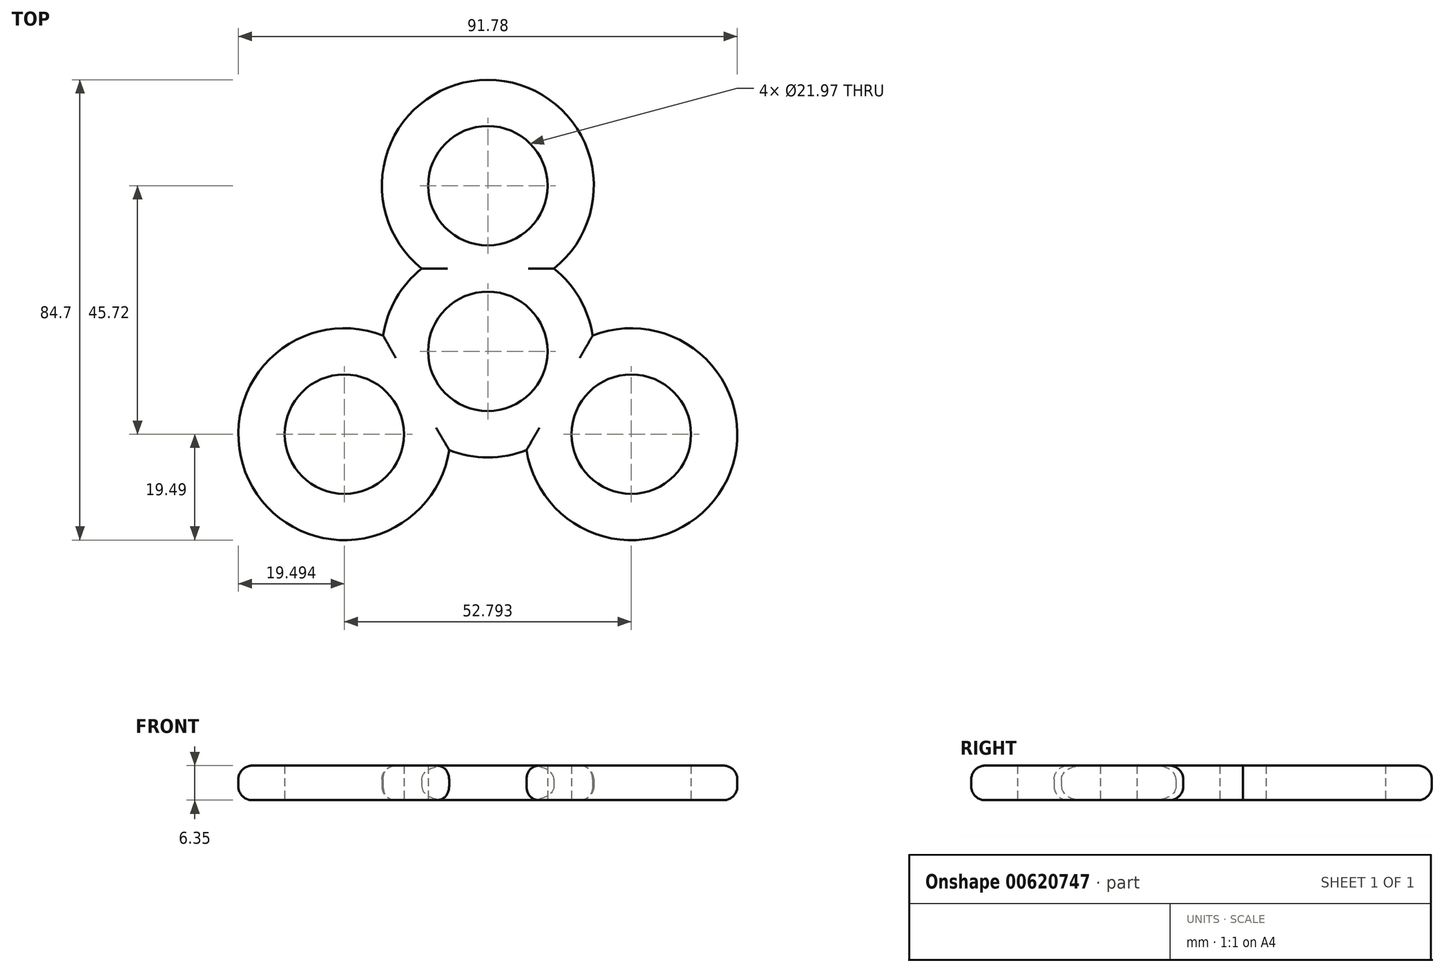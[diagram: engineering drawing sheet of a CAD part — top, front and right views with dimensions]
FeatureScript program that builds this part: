
annotation { "Feature Type Name" : "Feature", "Feature Type Description" : "" }
export const myFeature = defineFeature(function(context is Context, id is Id, definition is map)
    precondition{}
    {
        {
            var Q0;
            Q0=qCreatedBy(makeId("Top.planeOp"),FACE);
            var sketch = newSketch(context, id + "F0", { "sketchPlane" : qUnion([Q0])});
            skCircle(sketch, "E0", {"center": v(0, 0) * mm, "radius": 10.99 * mm});
            skLineSegment(sketch, "E1", {"start": v(0, 0) * mm, "end": v(0, 30.48) * mm});
            skLineSegment(sketch, "E2", {"start": v(0, 0) * mm, "end": v(-26.4, -15.24) * mm});
            skLineSegment(sketch, "E3", {"start": v(0, 0) * mm, "end": v(26.4, -15.24) * mm});
            skCircle(sketch, "E4", {"center": v(-26.4, -15.24) * mm, "radius": 10.99 * mm});
            skCircle(sketch, "E5", {"center": v(0, 30.48) * mm, "radius": 10.99 * mm});
            skCircle(sketch, "E6", {"center": v(26.4, -15.24) * mm, "radius": 10.99 * mm});
            skCircle(sketch, "E7", {"center": v(0, 0) * mm, "radius": 19.5 * mm});
            skCircle(sketch, "E8", {"center": v(-26.4, -15.24) * mm, "radius": 19.5 * mm});
            skCircle(sketch, "E9", {"center": v(26.4, -15.24) * mm, "radius": 19.5 * mm});
            skCircle(sketch, "E10", {"center": v(0, 30.48) * mm, "radius": 0.5 * mm});
            skCircle(sketch, "E11", {"center": v(0, 30.48) * mm, "radius": 19.5 * mm});
            skSolve(sketch);
        }
        {
            var Q0;
            Q0 = qSketchRegion(id + "F0", true);
            extrude(context, id + "F1", {"entities" : qUnion([Q0]), "depth" : 6.35 * mm, "offsetDistance" : 25.4 * mm});
        }
        {
            var Q0;
            Q0=makeQuery(id+"F1.opExtrude","CAP_EDGE",EDGE,{"disambiguationData":[OSD([sQuery(id+"F0.wireOp",EDGE,"E11")])],"isStart":false});
            var Q1;
            Q1=makeQuery(id+"F1.opExtrude","CAP_EDGE",EDGE,{"disambiguationData":[OSD([sQuery(id+"F0.wireOp",EDGE,"E8")])],"isStart":false});
            var Q2;
            {var subQ0=sQuery(id+"F0.wireOp",EDGE,"E7");Q2=makeQuery(id+"F1.opExtrude","CAP_EDGE",EDGE,{"disambiguationData":[OSD([subQ0]),TDD([makeQuery(id+"F0.imprint","IMPRINT",EDGE,{"disambiguationData":[TD([[makeQuery(id+"F0.imprint","INTERSECT",VERTEX,{"disambiguationData":[OD(1.0)],"derivedFrom":[subQ0,sQuery(id+"F0.wireOp",EDGE,"E8")]}),-1.0]])],"derivedFrom":subQ0})])],"isStart":false});}
            var Q3;
            {var subQ0=sQuery(id+"F0.wireOp",EDGE,"E7");Q3=makeQuery(id+"F1.opExtrude","CAP_EDGE",EDGE,{"disambiguationData":[OSD([subQ0]),TDD([makeQuery(id+"F0.imprint","IMPRINT",EDGE,{"disambiguationData":[TD([[makeQuery(id+"F0.imprint","INTERSECT",VERTEX,{"disambiguationData":[OD(0.0)],"derivedFrom":[subQ0,sQuery(id+"F0.wireOp",EDGE,"E11")]}),1.0]])],"derivedFrom":subQ0})])],"isStart":false});}
            var Q4;
            {var subQ0=sQuery(id+"F0.wireOp",EDGE,"E7");Q4=makeQuery(id+"F1.opExtrude","CAP_EDGE",EDGE,{"disambiguationData":[OSD([subQ0]),TDD([makeQuery(id+"F0.imprint","IMPRINT",EDGE,{"disambiguationData":[TD([[makeQuery(id+"F0.imprint","INTERSECT",VERTEX,{"disambiguationData":[OD(1.0)],"derivedFrom":[subQ0,sQuery(id+"F0.wireOp",EDGE,"E11")]}),-1.0]])],"derivedFrom":subQ0})])],"isStart":false});}
            var Q5;
            Q5=makeQuery(id+"F1.opExtrude","CAP_EDGE",EDGE,{"disambiguationData":[OSD([sQuery(id+"F0.wireOp",EDGE,"E9")])],"isStart":false});
            fillet(context, id + "F2", {"entities" : qUnion([Q0, Q1, Q2, Q3, Q4, Q5]), "radius" : 2.54 * mm, "tangentPropagation" : true, "allowEdgeOverflow" : false});
        }
        {
            var Q0;
            Q0=makeQuery(id+"F1.opExtrude","CAP_EDGE",EDGE,{"disambiguationData":[OSD([sQuery(id+"F0.wireOp",EDGE,"E9")])],"isStart":true});
            var Q1;
            Q1=makeQuery(id+"F1.opExtrude","CAP_EDGE",EDGE,{"disambiguationData":[OSD([sQuery(id+"F0.wireOp",EDGE,"E11")])],"isStart":true});
            var Q2;
            Q2=makeQuery(id+"F1.opExtrude","CAP_EDGE",EDGE,{"disambiguationData":[OSD([sQuery(id+"F0.wireOp",EDGE,"E8")])],"isStart":true});
            var Q3;
            {var subQ0=sQuery(id+"F0.wireOp",EDGE,"E7");Q3=makeQuery(id+"F1.opExtrude","CAP_EDGE",EDGE,{"disambiguationData":[OSD([subQ0]),TDD([makeQuery(id+"F0.imprint","IMPRINT",EDGE,{"disambiguationData":[TD([[makeQuery(id+"F0.imprint","INTERSECT",VERTEX,{"disambiguationData":[OD(1.0)],"derivedFrom":[subQ0,sQuery(id+"F0.wireOp",EDGE,"E11")]}),-1.0]])],"derivedFrom":subQ0})])],"isStart":true});}
            var Q4;
            {var subQ0=sQuery(id+"F0.wireOp",EDGE,"E7");Q4=makeQuery(id+"F1.opExtrude","CAP_EDGE",EDGE,{"disambiguationData":[OSD([subQ0]),TDD([makeQuery(id+"F0.imprint","IMPRINT",EDGE,{"disambiguationData":[TD([[makeQuery(id+"F0.imprint","INTERSECT",VERTEX,{"disambiguationData":[OD(1.0)],"derivedFrom":[subQ0,sQuery(id+"F0.wireOp",EDGE,"E8")]}),-1.0]])],"derivedFrom":subQ0})])],"isStart":true});}
            var Q5;
            {var subQ0=sQuery(id+"F0.wireOp",EDGE,"E7");Q5=makeQuery(id+"F1.opExtrude","CAP_EDGE",EDGE,{"disambiguationData":[OSD([subQ0]),TDD([makeQuery(id+"F0.imprint","IMPRINT",EDGE,{"disambiguationData":[TD([[makeQuery(id+"F0.imprint","INTERSECT",VERTEX,{"disambiguationData":[OD(0.0)],"derivedFrom":[subQ0,sQuery(id+"F0.wireOp",EDGE,"E11")]}),1.0]])],"derivedFrom":subQ0})])],"isStart":true});}
            fillet(context, id + "F3", {"entities" : qUnion([Q0, Q1, Q2, Q3, Q4, Q5]), "radius" : 2.54 * mm, "tangentPropagation" : true, "allowEdgeOverflow" : false});
        }
    });
